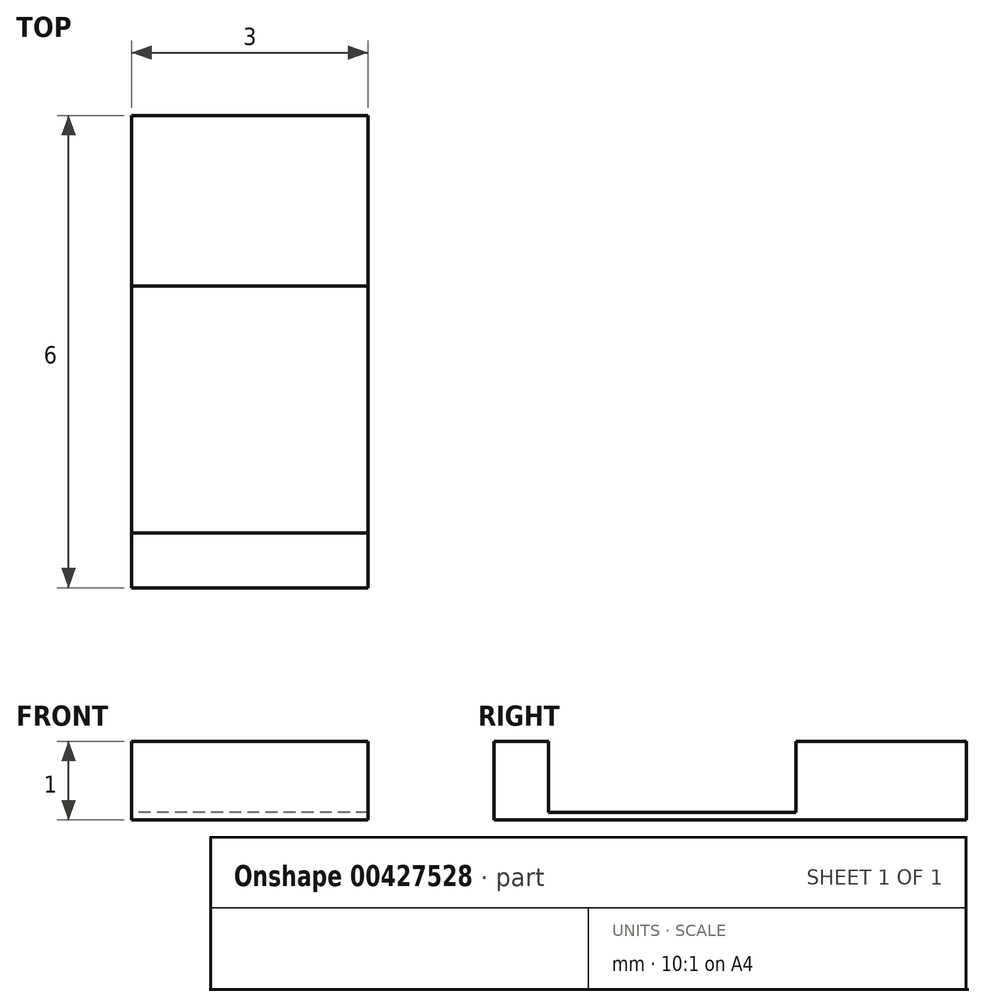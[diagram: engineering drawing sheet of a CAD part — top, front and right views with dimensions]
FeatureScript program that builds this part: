
annotation { "Feature Type Name" : "Feature", "Feature Type Description" : "" }
export const myFeature = defineFeature(function(context is Context, id is Id, definition is map)
    precondition{}
    {
        {
            var Q0;
            Q0=qCreatedBy(makeId("Right.planeOp"),FACE);
            var sketch = newSketch(context, id + "F0", { "sketchPlane" : qUnion([Q0])});
            skLineSegment(sketch, "E0.bottom", {"start": v(0, 1) * mm, "end": v(6, 1) * mm});
            skLineSegment(sketch, "E0.top", {"start": v(0, 0) * mm, "end": v(6, 0) * mm});
            skLineSegment(sketch, "E0.left", {"start": v(0, 1) * mm, "end": v(0, 0) * mm});
            skLineSegment(sketch, "E0.right", {"start": v(6, 1) * mm, "end": v(6, 0) * mm});
            skSolve(sketch);
        }
        {
            var Q0;
            Q0 = qSketchRegion(id + "F0", true);
            extrude(context, id + "F1", {"entities" : qUnion([Q0]), "endBound" : BoundingType.SYMMETRIC, "depth" : 3 * mm});
        }
        {
            var Q0;
            Q0=makeQuery(id+"F1.opExtrude","SWEPT_FACE",FACE,{"disambiguationData":[OSD([sQuery(id+"F0.wireOp",EDGE,"E0.bottom")])]});
            var sketch = newSketch(context, id + "F2", { "sketchPlane" : qUnion([Q0])});
            skLineSegment(sketch, "E1.bottom", {"start": v(1.5, 0.7) * mm, "end": v(-1.5, 0.7) * mm});
            skLineSegment(sketch, "E1.top", {"start": v(1.5, 3.84) * mm, "end": v(-1.5, 3.84) * mm});
            skLineSegment(sketch, "E1.left", {"start": v(1.5, 0.7) * mm, "end": v(1.5, 3.84) * mm});
            skLineSegment(sketch, "E1.right", {"start": v(-1.5, 0.7) * mm, "end": v(-1.5, 3.84) * mm});
            skSolve(sketch);
        }
        {
            var Q0;
            Q0 = qSketchRegion(id + "F2", true);
            extrude(context, id + "F3", {"entities" : qUnion([Q0]), "operationType" : NewBodyOperationType.REMOVE, "oppositeDirection" : true, "depth" : 0.9 * mm});
        }
    });
